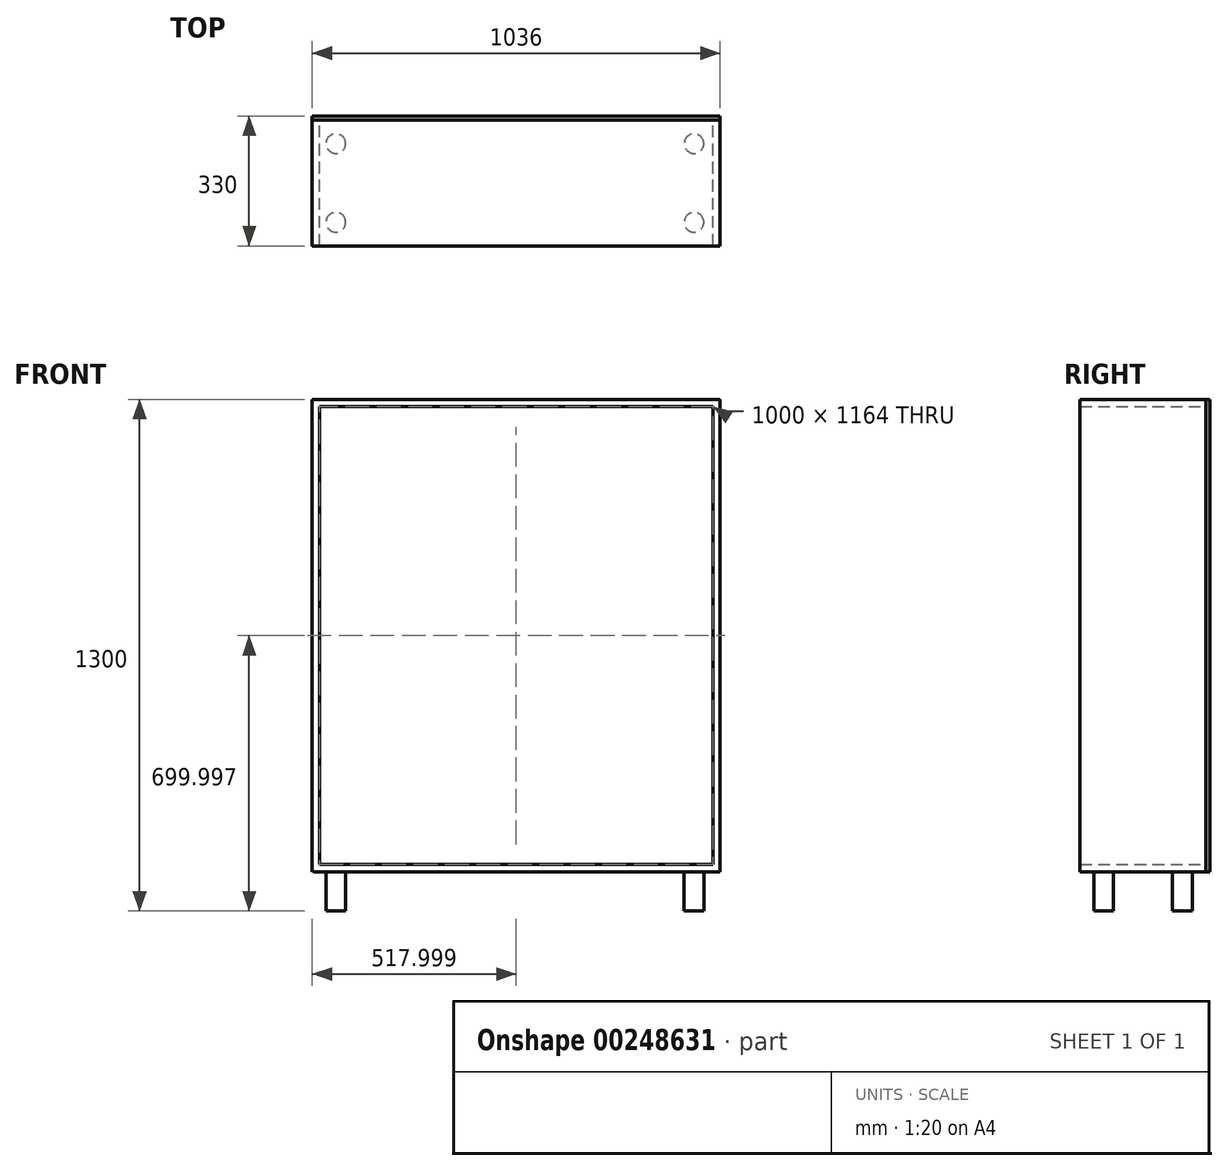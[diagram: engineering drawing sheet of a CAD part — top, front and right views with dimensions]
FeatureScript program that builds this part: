
annotation { "Feature Type Name" : "Feature", "Feature Type Description" : "" }
export const myFeature = defineFeature(function(context is Context, id is Id, definition is map)
    precondition{}
    {
        {
            var Q0;
            Q0=qCreatedBy(makeId("Front.planeOp"),FACE);
            var sketch = newSketch(context, id + "F0", { "sketchPlane" : qUnion([Q0])});
            skLineSegment(sketch, "E0.bottom", {"start": v(-516.18, 598.7) * mm, "end": v(519.82, 598.7) * mm});
            skLineSegment(sketch, "E0.top", {"start": v(-516.18, -601.3) * mm, "end": v(519.82, -601.3) * mm});
            skLineSegment(sketch, "E0.left", {"start": v(-516.18, 598.7) * mm, "end": v(-516.18, -601.3) * mm});
            skLineSegment(sketch, "E0.right", {"start": v(519.82, 598.7) * mm, "end": v(519.82, -601.3) * mm});
            skLineSegment(sketch, "E1.0", {"start": v(501.82, 580.7) * mm, "end": v(501.82, -583.3) * mm});
            skLineSegment(sketch, "E1.1", {"start": v(-498.18, 580.7) * mm, "end": v(501.82, 580.7) * mm});
            skLineSegment(sketch, "E1.2", {"start": v(-498.18, 580.7) * mm, "end": v(-498.18, -583.3) * mm});
            skLineSegment(sketch, "E1.3", {"start": v(-498.18, -583.3) * mm, "end": v(501.82, -583.3) * mm});
            skSolve(sketch);
        }
        {
            var Q0;
            Q0 = qSketchRegion(id + "F0", true);
            extrude(context, id + "F1", {"entities" : qUnion([Q0]), "depth" : 320 * mm});
        }
        {
            var Q0;
            Q0=makeQuery(id+"F1.opExtrude","CAP_FACE",FACE,{"disambiguationData":[OSD([sQuery(id+"F0.wireOp",EDGE,"E0.bottom"),sQuery(id+"F0.wireOp",EDGE,"E0.top"),sQuery(id+"F0.wireOp",EDGE,"E0.left"),sQuery(id+"F0.wireOp",EDGE,"E0.right"),sQuery(id+"F0.wireOp",EDGE,"E1.0"),sQuery(id+"F0.wireOp",EDGE,"E1.1"),sQuery(id+"F0.wireOp",EDGE,"E1.2"),sQuery(id+"F0.wireOp",EDGE,"E1.3")])],"isStart":true});
            var sketch = newSketch(context, id + "F2", { "sketchPlane" : qUnion([Q0])});
            skLineSegment(sketch, "E2.bottom", {"start": v(516.18, 598.7) * mm, "end": v(-519.82, 598.7) * mm});
            skLineSegment(sketch, "E2.top", {"start": v(516.18, -601.3) * mm, "end": v(-519.82, -601.3) * mm});
            skLineSegment(sketch, "E2.left", {"start": v(516.18, 598.7) * mm, "end": v(516.18, -601.3) * mm});
            skLineSegment(sketch, "E2.right", {"start": v(-519.82, 598.7) * mm, "end": v(-519.82, -601.3) * mm});
            skSolve(sketch);
        }
        {
            var Q0;
            Q0 = qSketchRegion(id + "F2", true);
            extrude(context, id + "F3", {"entities" : qUnion([Q0]), "depth" : 10 * mm});
        }
        {
            var Q0;
            Q0=makeQuery(id+"F1.opExtrude","SWEPT_FACE",FACE,{"disambiguationData":[OSD([sQuery(id+"F0.wireOp",EDGE,"E0.top")])]});
            var sketch = newSketch(context, id + "F4", { "sketchPlane" : qUnion([Q0])});
            skLineSegment(sketch, "E3.bottom", {"start": v(-516.18, 320) * mm, "end": v(-456.18, 320) * mm, "construction": true});
            skLineSegment(sketch, "E3.top", {"start": v(-516.18, 260) * mm, "end": v(-456.18, 260) * mm, "construction": true});
            skLineSegment(sketch, "E3.left", {"start": v(-516.18, 320) * mm, "end": v(-516.18, 260) * mm, "construction": true});
            skLineSegment(sketch, "E3.right", {"start": v(-456.18, 320) * mm, "end": v(-456.18, 260) * mm, "construction": true});
            skCircle(sketch, "E4", {"center": v(-456.18, 260) * mm, "radius": 25 * mm});
            skCircle(sketch, "E5.0.1.0", {"center": v(-456.18, 60) * mm, "radius": 25 * mm});
            skCircle(sketch, "E5.1.0.0", {"center": v(453.82, 260) * mm, "radius": 25 * mm});
            skCircle(sketch, "E5.1.1.0", {"center": v(453.82, 60) * mm, "radius": 25 * mm});
            skLineSegment(sketch, "E5.direction1", {"start": v(-456.18, 260) * mm, "end": v(453.82, 260) * mm, "construction": true});
            skLineSegment(sketch, "E5.direction2", {"start": v(-456.18, 260) * mm, "end": v(-456.18, 60) * mm, "construction": true});
            skSolve(sketch);
        }
        {
            var Q0;
            Q0 = qSketchRegion(id + "F4", true);
            extrude(context, id + "F5", {"entities" : qUnion([Q0]), "depth" : 100 * mm});
        }
        {
            var Q0;
            Q0=makeQuery(id+"F1.opExtrude","SWEPT_EDGE",EDGE,{"disambiguationData":[OSD([sQuery(id+"F0.wireOp",EDGE,"E0.bottom"),sQuery(id+"F0.wireOp",EDGE,"E0.left")])]});
            var Q1;
            Q1=makeQuery(id+"F1.opExtrude","SWEPT_EDGE",EDGE,{"disambiguationData":[OSD([sQuery(id+"F0.wireOp",EDGE,"E0.top"),sQuery(id+"F0.wireOp",EDGE,"E0.left")])]});
            var Q2;
            Q2=makeQuery(id+"F1.opExtrude","SWEPT_EDGE",EDGE,{"disambiguationData":[OSD([sQuery(id+"F0.wireOp",EDGE,"E0.top"),sQuery(id+"F0.wireOp",EDGE,"E0.right")])]});
            var Q3;
            Q3=makeQuery(id+"F1.opExtrude","SWEPT_EDGE",EDGE,{"disambiguationData":[OSD([sQuery(id+"F0.wireOp",EDGE,"E0.bottom"),sQuery(id+"F0.wireOp",EDGE,"E0.right")])]});
            fillet(context, id + "F6", {"entities" : qUnion([Q0, Q1, Q2, Q3]), "radius" : 5 * mm, "tangentPropagation" : true, "allowEdgeOverflow" : false});
        }
    });
